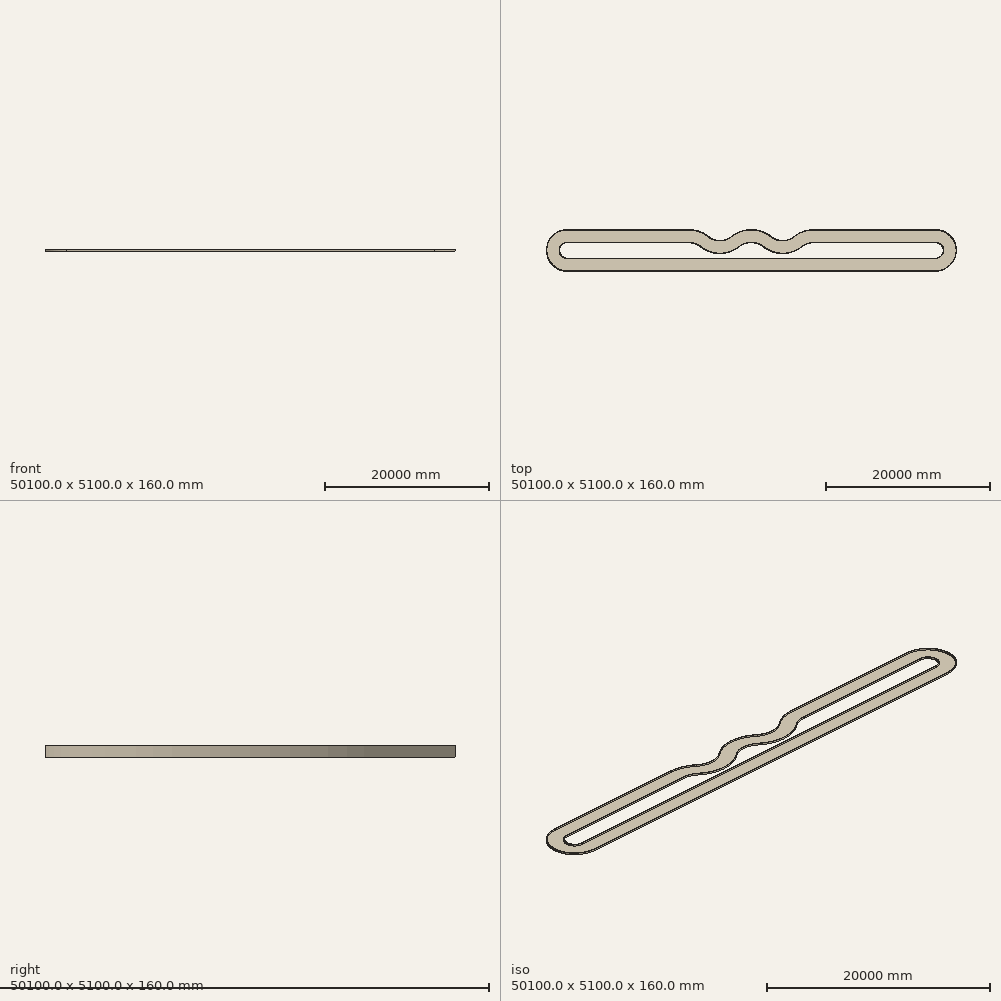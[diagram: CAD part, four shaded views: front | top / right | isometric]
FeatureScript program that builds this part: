
annotation { "Feature Type Name" : "Feature", "Feature Type Description" : "" }
export const myFeature = defineFeature(function(context is Context, id is Id, definition is map)
    precondition{}
    {
        {
            var Q0;
            Q0=qCreatedBy(makeId("Top.planeOp"),FACE);
            var sketch = newSketch(context, id + "F0", { "sketchPlane" : qUnion([Q0])});
            skLineSegment(sketch, "E0", {"start": v(0, -1750) * mm, "end": v(22500, -1750) * mm});
            skArc(sketch, "E1", {"start": v(22500, -1750) * mm, "mid": v(24250, 0) * mm, "end": v(22500, 1750) * mm});
            skLineSegment(sketch, "E2", {"start": v(0, 1750) * mm, "end": v(22500, 1750) * mm, "construction": true});
            skArc(sketch, "E3", {"start": v(1915, 1082.3) * mm, "mid": v(1014.03, 1578.29) * mm, "end": v(0, 1750) * mm});
            skArc(sketch, "E4", {"start": v(1915, 1082.3) * mm, "mid": v(3830, 414.6) * mm, "end": v(5745, 1082.3) * mm});
            skArc(sketch, "E5", {"start": v(7660, 1750) * mm, "mid": v(6645.97, 1578.29) * mm, "end": v(5745, 1082.3) * mm});
            skLineSegment(sketch, "E6", {"start": v(0, 0) * mm, "end": v(0, -1750) * mm, "construction": true});
            skLineSegment(sketch, "E7.MirrorCS", {"start": v(0, -1750) * mm, "end": v(-22500, -1750) * mm});
            skArc(sketch, "E8.MirrorCS", {"start": v(-1915, 1082.3) * mm, "mid": v(-3830, 414.6) * mm, "end": v(-5745, 1082.3) * mm});
            skArc(sketch, "E9.MirrorCS", {"start": v(-22500, -1750) * mm, "mid": v(-24250, 0) * mm, "end": v(-22500, 1750) * mm});
            skArc(sketch, "E10.MirrorCS", {"start": v(-1915, 1082.3) * mm, "mid": v(-1014.03, 1578.29) * mm, "end": v(0, 1750) * mm});
            skLineSegment(sketch, "E11.MirrorCS", {"start": v(0, 1750) * mm, "end": v(-22500, 1750) * mm, "construction": true});
            skArc(sketch, "E12.MirrorCS", {"start": v(-7660, 1750) * mm, "mid": v(-6645.97, 1578.29) * mm, "end": v(-5745, 1082.3) * mm});
            skLineSegment(sketch, "E13", {"start": v(-22500, 1750) * mm, "end": v(-7660, 1750) * mm});
            skLineSegment(sketch, "E14", {"start": v(7660, 1750) * mm, "end": v(22500, 1750) * mm});
            skSolve(sketch);
        }
        {
            var Q0;
            Q0=qCreatedBy(makeId("Right.planeOp"),FACE);
            var sketch = newSketch(context, id + "F1", { "sketchPlane" : qUnion([Q0])});
            skLineSegment(sketch, "E15", {"start": v(-1750, -10) * mm, "end": v(-850, -10) * mm});
            skLineSegment(sketch, "E16", {"start": v(-850, -10) * mm, "end": v(-850, 150) * mm});
            skLineSegment(sketch, "E17", {"start": v(-850, 150) * mm, "end": v(-1000, 150) * mm});
            skLineSegment(sketch, "E18", {"start": v(-1000, 150) * mm, "end": v(-1000, 0) * mm});
            skLineSegment(sketch, "E19", {"start": v(-1000, 0) * mm, "end": v(-1655, 0) * mm});
            skLineSegment(sketch, "E20", {"start": v(-1655, 0) * mm, "end": v(-1655, 0.1) * mm});
            skLineSegment(sketch, "E21", {"start": v(-1655, 0.1) * mm, "end": v(-1730, 0.1) * mm});
            skLineSegment(sketch, "E22", {"start": v(-1730, 0.1) * mm, "end": v(-1730, 0.2) * mm});
            skLineSegment(sketch, "E23", {"start": v(-1730, 0.2) * mm, "end": v(-1750, 0.2) * mm});
            skLineSegment(sketch, "E24", {"start": v(-1750, -10) * mm, "end": v(-1750, 0.2) * mm, "construction": true});
            skLineSegment(sketch, "E25.MirrorCS", {"start": v(-1770, 0.1) * mm, "end": v(-1770, 0.2) * mm});
            skLineSegment(sketch, "E26.MirrorCS", {"start": v(-1845, 0) * mm, "end": v(-1845, 0.1) * mm});
            skLineSegment(sketch, "E27.MirrorCS", {"start": v(-1770, 0.2) * mm, "end": v(-1750, 0.2) * mm});
            skLineSegment(sketch, "E28.MirrorCS", {"start": v(-2650, -10) * mm, "end": v(-2650, 150) * mm});
            skLineSegment(sketch, "E29.MirrorCS", {"start": v(-1750, -10) * mm, "end": v(-2650, -10) * mm});
            skLineSegment(sketch, "E30.MirrorCS", {"start": v(-2650, 150) * mm, "end": v(-2500, 150) * mm});
            skLineSegment(sketch, "E31.MirrorCS", {"start": v(-2500, 0) * mm, "end": v(-1845, 0) * mm});
            skLineSegment(sketch, "E32.MirrorCS", {"start": v(-2500, 150) * mm, "end": v(-2500, 0) * mm});
            skLineSegment(sketch, "E33.MirrorCS", {"start": v(-1845, 0.1) * mm, "end": v(-1770, 0.1) * mm});
            skSolve(sketch);
        }
        {
            var Q0;
            Q0=qCreatedBy(makeId("Right.planeOp"),FACE);
            var sketch = newSketch(context, id + "F2", { "sketchPlane" : qUnion([Q0])});
            skLineSegment(sketch, "E34", {"start": v(-1750, -10) * mm, "end": v(-950, -10) * mm});
            skLineSegment(sketch, "E35", {"start": v(-950, -10) * mm, "end": v(-950, 150) * mm});
            skLineSegment(sketch, "E36", {"start": v(-950, 150) * mm, "end": v(-1000, 150) * mm});
            skLineSegment(sketch, "E37", {"start": v(-1000, 150) * mm, "end": v(-1000, 0) * mm});
            skLineSegment(sketch, "E38", {"start": v(-1000, 0) * mm, "end": v(-1750, 0) * mm});
            skLineSegment(sketch, "E39", {"start": v(-1750, 0) * mm, "end": v(-1750, -10) * mm, "construction": true});
            skLineSegment(sketch, "E40.MirrorCS", {"start": v(-2500, 0) * mm, "end": v(-1750, 0) * mm});
            skLineSegment(sketch, "E41.MirrorCS", {"start": v(-1750, -10) * mm, "end": v(-2550, -10) * mm});
            skLineSegment(sketch, "E42.MirrorCS", {"start": v(-2550, 150) * mm, "end": v(-2500, 150) * mm});
            skLineSegment(sketch, "E43.MirrorCS", {"start": v(-2500, 150) * mm, "end": v(-2500, 0) * mm});
            skLineSegment(sketch, "E44.MirrorCS", {"start": v(-2550, -10) * mm, "end": v(-2550, 150) * mm});
            skSolve(sketch);
        }
        {
            var Q0;
            Q0=qCreatedBy(makeId("Right.planeOp"),FACE);
            var sketch = newSketch(context, id + "F3", { "sketchPlane" : qUnion([Q0])});
            skLineSegment(sketch, "E45.bottom", {"start": v(-1750, -1) * mm, "end": v(-1675, -1) * mm});
            skLineSegment(sketch, "E45.top", {"start": v(-1750, 0) * mm, "end": v(-1675, 0) * mm});
            skLineSegment(sketch, "E45.left", {"start": v(-1750, -1) * mm, "end": v(-1750, 0) * mm, "construction": true});
            skLineSegment(sketch, "E45.right", {"start": v(-1675, -1) * mm, "end": v(-1675, 0) * mm});
            skLineSegment(sketch, "E46.MirrorCS", {"start": v(-1825, -1) * mm, "end": v(-1825, 0) * mm});
            skLineSegment(sketch, "E47.MirrorCS", {"start": v(-1750, 0) * mm, "end": v(-1825, 0) * mm});
            skLineSegment(sketch, "E48.MirrorCS", {"start": v(-1750, -1) * mm, "end": v(-1825, -1) * mm});
            skSolve(sketch);
        }
        {
            var Q0;
            Q0=qCreatedBy(makeId("Right.planeOp"),FACE);
            var sketch = newSketch(context, id + "F4", { "sketchPlane" : qUnion([Q0])});
            skLineSegment(sketch, "E49.bottom", {"start": v(-1750, 0) * mm, "end": v(-1730, 0) * mm});
            skLineSegment(sketch, "E49.top", {"start": v(-1750, -1) * mm, "end": v(-1730, -1) * mm});
            skLineSegment(sketch, "E49.left", {"start": v(-1750, 0) * mm, "end": v(-1750, -1) * mm});
            skLineSegment(sketch, "E49.right", {"start": v(-1730, 0) * mm, "end": v(-1730, -1) * mm});
            skLineSegment(sketch, "E50.MirrorCS", {"start": v(-1750, 0) * mm, "end": v(-1770, 0) * mm});
            skLineSegment(sketch, "E51.MirrorCS", {"start": v(-1750, -1) * mm, "end": v(-1770, -1) * mm});
            skLineSegment(sketch, "E52.MirrorCS", {"start": v(-1770, 0) * mm, "end": v(-1770, -1) * mm});
            skSolve(sketch);
        }
        {
            var Q0;
            Q0 = qSketchRegion(id + "F2", true);
            var Q1;
            Q1 = qConstructionFilter(qBodyType(qCreatedBy(id + "F0" ,EDGE), BodyType.WIRE), ConstructionObject.NO);
            sweep(context, id + "F5", {"profiles" : qUnion([Q0]), "path" : qUnion([Q1])});
        }
    });
